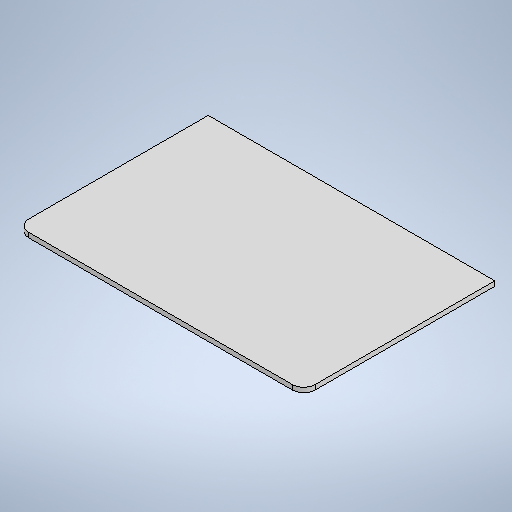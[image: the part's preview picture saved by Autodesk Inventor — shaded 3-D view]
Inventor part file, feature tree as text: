
AUTODESK INVENTOR PART (.ipt)
format: ipt  version: 2025 (Build 290162010, 162A)  size: 226,304 bytes
history: native  units: mm
features: sheet_metal_op x1, chamfer x1, sketch x1, other x1
ambient origin geometry x8: Origin, YZ Plane, XZ Plane, XY Plane, X Axis, Y Axis, Z Axis, Center Point
bodies: Solid1 (feature_tree)
feature tree (4):
  sheet_metal_op  "Face1"
  chamfer  "Corner Round2"
  sketch  "Sketch1"  dims[d0=120.0mm d1=80.0mm d2=2.0mm d4=4.75mm]
  other  "Plate1"
